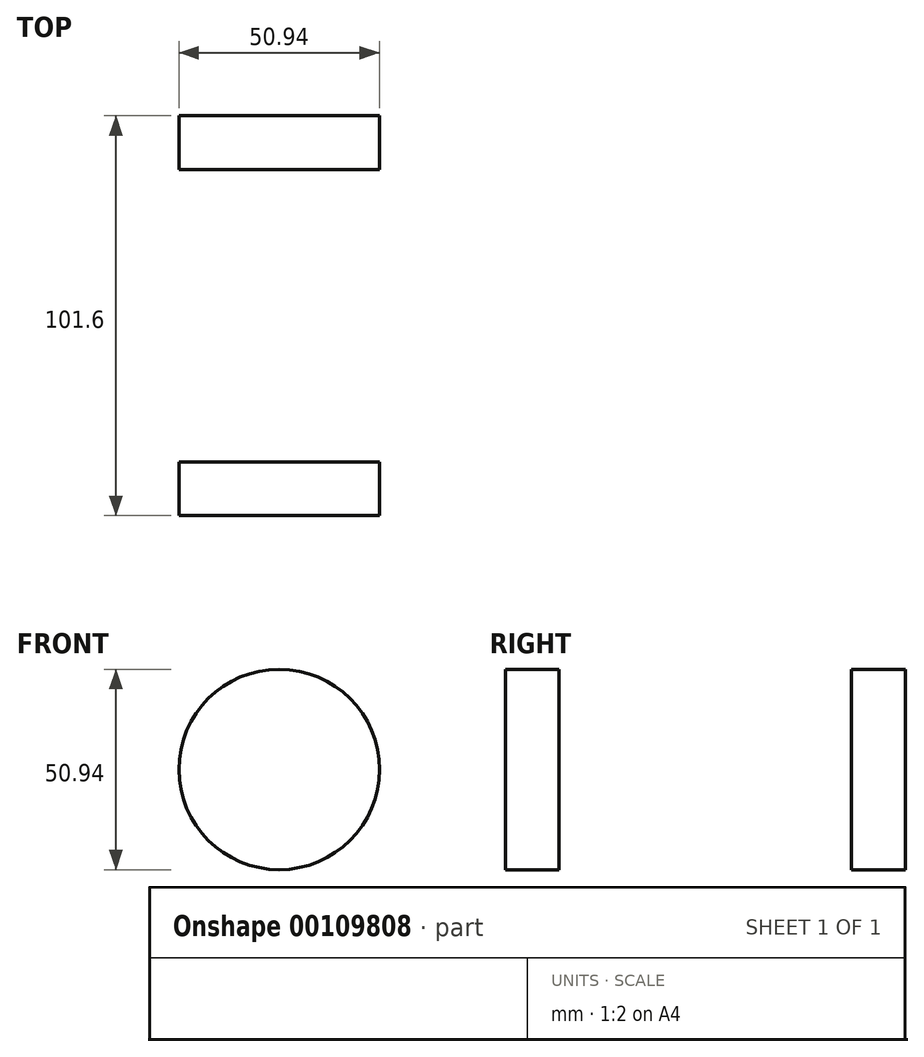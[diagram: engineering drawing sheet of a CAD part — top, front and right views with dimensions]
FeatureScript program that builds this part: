
annotation { "Feature Type Name" : "Feature", "Feature Type Description" : "" }
export const myFeature = defineFeature(function(context is Context, id is Id, definition is map)
    precondition{}
    {
        {
            var Q0;
            Q0=qCreatedBy(makeId("Front.planeOp"),FACE);
            var sketch = newSketch(context, id + "F0", { "sketchPlane" : qUnion([Q0])});
            skCircle(sketch, "E0", {"center": v(0, 0) * mm, "radius": 25.47 * mm});
            skSolve(sketch);
        }
        {
            var Q0;
            Q0=makeQuery(id+"F0.imprint","IMPRINT",FACE,{"disambiguationData":[TD([[makeQuery(id+"F0.imprint","IMPRINT",EDGE,{"derivedFrom":sQuery(id+"F0.wireOp",EDGE,"E0")}),1.0]])]});
            extrude(context, id + "F1", {"entities" : qUnion([Q0]), "endBound" : BoundingType.SYMMETRIC, "depth" : 101.6 * mm});
        }
        {
            var Q0;
            Q0=qCreatedBy(makeId("Right.planeOp"),FACE);
            var sketch = newSketch(context, id + "F2", { "sketchPlane" : qUnion([Q0])});
            skLineSegment(sketch, "E1.bottom", {"start": v(37.13, 36.83) * mm, "end": v(-37.13, 36.83) * mm});
            skLineSegment(sketch, "E1.top", {"start": v(37.13, -36.83) * mm, "end": v(-37.13, -36.83) * mm});
            skLineSegment(sketch, "E1.left", {"start": v(37.13, 36.83) * mm, "end": v(37.13, -36.83) * mm});
            skLineSegment(sketch, "E1.right", {"start": v(-37.13, 36.83) * mm, "end": v(-37.13, -36.83) * mm});
            skPoint(sketch, "E1.middle", {"position": v(0, 0) * mm});
            skSolve(sketch);
        }
        {
            var Q0;
            Q0 = qSketchRegion(id + "F2", true);
            extrude(context, id + "F3", {"entities" : qUnion([Q0]), "operationType" : NewBodyOperationType.REMOVE, "endBound" : BoundingType.SYMMETRIC, "oppositeDirection" : true, "depth" : 101.6 * mm});
        }
    });
